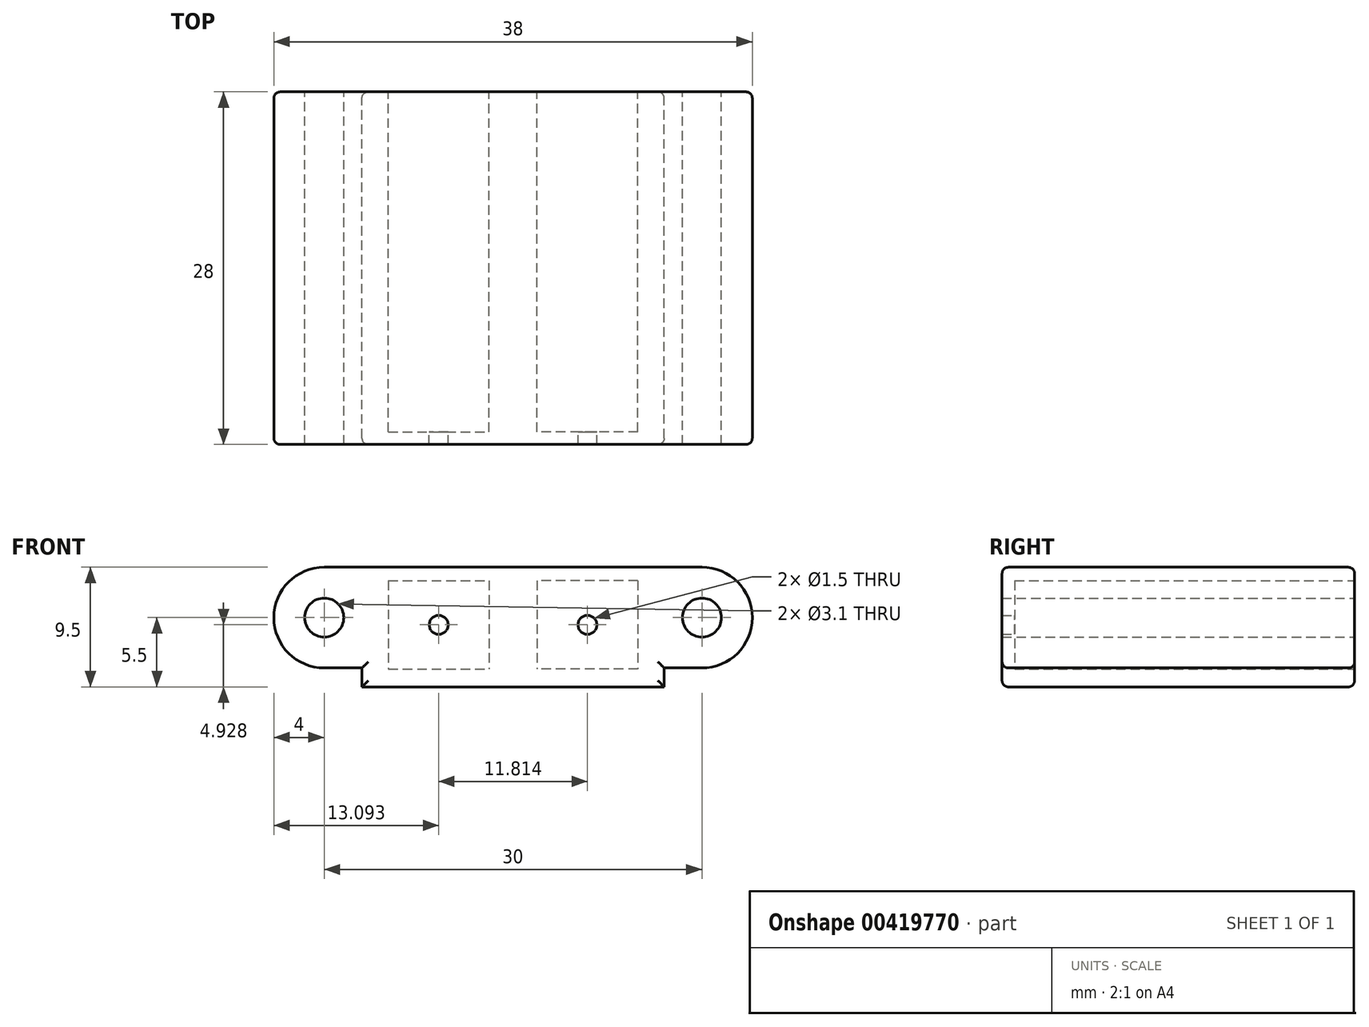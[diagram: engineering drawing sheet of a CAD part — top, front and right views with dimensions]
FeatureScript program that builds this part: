
annotation { "Feature Type Name" : "Feature", "Feature Type Description" : "" }
export const myFeature = defineFeature(function(context is Context, id is Id, definition is map)
    precondition{}
    {
        {
            var Q0;
            Q0=qCreatedBy(makeId("Front.planeOp"),FACE);
            var sketch = newSketch(context, id + "F0", { "sketchPlane" : qUnion([Q0])});
            skCircle(sketch, "E0", {"center": v(-15, 0) * mm, "radius": 1.55 * mm});
            skCircle(sketch, "E1", {"center": v(15, 0) * mm, "radius": 1.55 * mm});
            skArc(sketch, "E2", {"start": v(15, 4) * mm, "mid": v(19, 0) * mm, "end": v(15, -4) * mm});
            skLineSegment(sketch, "E3", {"start": v(15, 4) * mm, "end": v(0, 4) * mm});
            skArc(sketch, "E4", {"start": v(-15, 4) * mm, "mid": v(-19, 0) * mm, "end": v(-15, -4) * mm});
            skLineSegment(sketch, "E5", {"start": v(15, -4) * mm, "end": v(12, -4) * mm});
            skLineSegment(sketch, "E6", {"start": v(12, -5) * mm, "end": v(12, -5.5) * mm});
            skLineSegment(sketch, "E7", {"start": v(-12, -5.5) * mm, "end": v(-12, -5) * mm});
            skLineSegment(sketch, "E8", {"start": v(12, -5.5) * mm, "end": v(0, -5.5) * mm});
            skLineSegment(sketch, "E9", {"start": v(0, 4) * mm, "end": v(-15, 4) * mm});
            skLineSegment(sketch, "E10", {"start": v(0, -5.5) * mm, "end": v(-12, -5.5) * mm});
            skLineSegment(sketch, "E11", {"start": v(-12, -4) * mm, "end": v(-15, -4) * mm});
            skLineSegment(sketch, "E12", {"start": v(12, -5) * mm, "end": v(12, -4) * mm});
            skLineSegment(sketch, "E13", {"start": v(-12, -5) * mm, "end": v(-12, -4) * mm});
            skLineSegment(sketch, "E14.bottom", {"start": v(-9.9, 2.93) * mm, "end": v(-1.9, 2.93) * mm});
            skLineSegment(sketch, "E14.top", {"start": v(-9.9, -4.07) * mm, "end": v(-1.9, -4.07) * mm});
            skLineSegment(sketch, "E14.left", {"start": v(-9.9, 2.93) * mm, "end": v(-9.9, -4.07) * mm});
            skLineSegment(sketch, "E14.right", {"start": v(-1.9, 2.93) * mm, "end": v(-1.9, -4.07) * mm});
            skLineSegment(sketch, "E15.MirrorCS", {"start": v(9.9, 2.93) * mm, "end": v(9.9, -4.07) * mm});
            skLineSegment(sketch, "E16.MirrorCS", {"start": v(9.9, -4.07) * mm, "end": v(1.9, -4.07) * mm});
            skLineSegment(sketch, "E17.MirrorCS", {"start": v(9.9, 2.93) * mm, "end": v(1.9, 2.93) * mm});
            skLineSegment(sketch, "E18.MirrorCS", {"start": v(1.9, 2.93) * mm, "end": v(1.9, -4.07) * mm});
            skPoint(sketch, "E19.centerSnap0", {"position": v(5.9, 2.93) * mm});
            skCircle(sketch, "E20", {"center": v(5.9, -0.57) * mm, "radius": 0.75 * mm});
            skPoint(sketch, "E20.centerSnap0", {"position": v(1.9, -0.57) * mm});
            skCircle(sketch, "E21", {"center": v(-5.9, -0.57) * mm, "radius": 0.75 * mm});
            skPoint(sketch, "E21.centerSnap0", {"position": v(-1.9, -0.57) * mm});
            skPoint(sketch, "E21.centerSnap1", {"position": v(-5.9, 2.93) * mm});
            skSolve(sketch);
        }
        {
            var Q0;
            Q0=makeQuery(id+"F0.imprint","IMPRINT",FACE,{"disambiguationData":[TD([[makeQuery(id+"F0.imprint","IMPRINT",EDGE,{"derivedFrom":sQuery(id+"F0.wireOp",EDGE,"E0")}),-1.0]])]});
            var Q1;
            Q1=makeQuery(id+"F0.imprint","IMPRINT",FACE,{"disambiguationData":[TD([[makeQuery(id+"F0.imprint","IMPRINT",EDGE,{"derivedFrom":sQuery(id+"F0.wireOp",EDGE,"E15.MirrorCS")}),-1.0]])]});
            var Q2;
            Q2=makeQuery(id+"F0.imprint","IMPRINT",FACE,{"disambiguationData":[TD([[makeQuery(id+"F0.imprint","IMPRINT",EDGE,{"derivedFrom":sQuery(id+"F0.wireOp",EDGE,"E14.bottom")}),-1.0]])]});
            extrude(context, id + "F1", {"entities" : qUnion([Q0, Q1, Q2]), "depth" : 28 * mm});
        }
        {
            var Q0;
            Q0=makeQuery(id+"F0.imprint","IMPRINT",FACE,{"disambiguationData":[TD([[makeQuery(id+"F0.imprint","IMPRINT",EDGE,{"derivedFrom":sQuery(id+"F0.wireOp",EDGE,"E15.MirrorCS")}),-1.0]])]});
            var Q1;
            Q1=makeQuery(id+"F0.imprint","IMPRINT",FACE,{"disambiguationData":[TD([[makeQuery(id+"F0.imprint","IMPRINT",EDGE,{"derivedFrom":sQuery(id+"F0.wireOp",EDGE,"E14.bottom")}),-1.0]])]});
            extrude(context, id + "F2", {"entities" : qUnion([Q0, Q1]), "operationType" : NewBodyOperationType.REMOVE, "depth" : 27 * mm});
        }
        {
            var Q0;
            Q0=makeQuery(id+"F1.opExtrude","CAP_EDGE",EDGE,{"disambiguationData":[OSD([sQuery(id+"F0.wireOp",EDGE,"E3"),sQuery(id+"F0.wireOp",EDGE,"E9")])],"isStart":true});
            var Q1;
            Q1=makeQuery(id+"F1.opExtrude","CAP_EDGE",EDGE,{"disambiguationData":[OSD([sQuery(id+"F0.wireOp",EDGE,"E11")])],"isStart":true});
            var Q2;
            Q2=makeQuery(id+"F1.opExtrude","CAP_EDGE",EDGE,{"disambiguationData":[OSD([sQuery(id+"F0.wireOp",EDGE,"E8"),sQuery(id+"F0.wireOp",EDGE,"E10")])],"isStart":true});
            var Q3;
            Q3=makeQuery(id+"F1.opExtrude","CAP_EDGE",EDGE,{"disambiguationData":[OSD([sQuery(id+"F0.wireOp",EDGE,"E7"),sQuery(id+"F0.wireOp",EDGE,"E13")])],"isStart":true});
            var Q4;
            Q4=makeQuery(id+"F1.opExtrude","CAP_EDGE",EDGE,{"disambiguationData":[OSD([sQuery(id+"F0.wireOp",EDGE,"E6"),sQuery(id+"F0.wireOp",EDGE,"E12")])],"isStart":true});
            var Q5;
            Q5=makeQuery(id+"F1.opExtrude","CAP_EDGE",EDGE,{"disambiguationData":[OSD([sQuery(id+"F0.wireOp",EDGE,"E5")])],"isStart":true});
            var Q6;
            Q6=makeQuery(id+"F1.opExtrude","CAP_EDGE",EDGE,{"disambiguationData":[OSD([sQuery(id+"F0.wireOp",EDGE,"E2")])],"isStart":true});
            var Q7;
            Q7=makeQuery(id+"F1.opExtrude","CAP_EDGE",EDGE,{"disambiguationData":[OSD([sQuery(id+"F0.wireOp",EDGE,"E4")])],"isStart":true});
            fillet(context, id + "F3", {"entities" : qUnion([Q0, Q1, Q2, Q3, Q4, Q5, Q6, Q7]), "radius" : 0.5 * mm, "tangentPropagation" : true, "allowEdgeOverflow" : false});
        }
        {
            var Q0;
            Q0=makeQuery(id+"F1.opExtrude","CAP_EDGE",EDGE,{"disambiguationData":[OSD([sQuery(id+"F0.wireOp",EDGE,"E3"),sQuery(id+"F0.wireOp",EDGE,"E9")])],"isStart":false});
            var Q1;
            Q1=makeQuery(id+"F1.opExtrude","CAP_EDGE",EDGE,{"disambiguationData":[OSD([sQuery(id+"F0.wireOp",EDGE,"E4")])],"isStart":false});
            var Q2;
            Q2=makeQuery(id+"F1.opExtrude","CAP_EDGE",EDGE,{"disambiguationData":[OSD([sQuery(id+"F0.wireOp",EDGE,"E11")])],"isStart":false});
            var Q3;
            Q3=makeQuery(id+"F1.opExtrude","CAP_EDGE",EDGE,{"disambiguationData":[OSD([sQuery(id+"F0.wireOp",EDGE,"E7"),sQuery(id+"F0.wireOp",EDGE,"E13")])],"isStart":false});
            var Q4;
            Q4=makeQuery(id+"F1.opExtrude","CAP_EDGE",EDGE,{"disambiguationData":[OSD([sQuery(id+"F0.wireOp",EDGE,"E8"),sQuery(id+"F0.wireOp",EDGE,"E10")])],"isStart":false});
            var Q5;
            Q5=makeQuery(id+"F1.opExtrude","CAP_EDGE",EDGE,{"disambiguationData":[OSD([sQuery(id+"F0.wireOp",EDGE,"E6"),sQuery(id+"F0.wireOp",EDGE,"E12")])],"isStart":false});
            var Q6;
            Q6=makeQuery(id+"F1.opExtrude","CAP_EDGE",EDGE,{"disambiguationData":[OSD([sQuery(id+"F0.wireOp",EDGE,"E5")])],"isStart":false});
            var Q7;
            Q7=makeQuery(id+"F1.opExtrude","CAP_EDGE",EDGE,{"disambiguationData":[OSD([sQuery(id+"F0.wireOp",EDGE,"E2")])],"isStart":false});
            fillet(context, id + "F4", {"entities" : qUnion([Q0, Q1, Q2, Q3, Q4, Q5, Q6, Q7]), "radius" : 0.5 * mm, "tangentPropagation" : true, "allowEdgeOverflow" : false});
        }
    });
